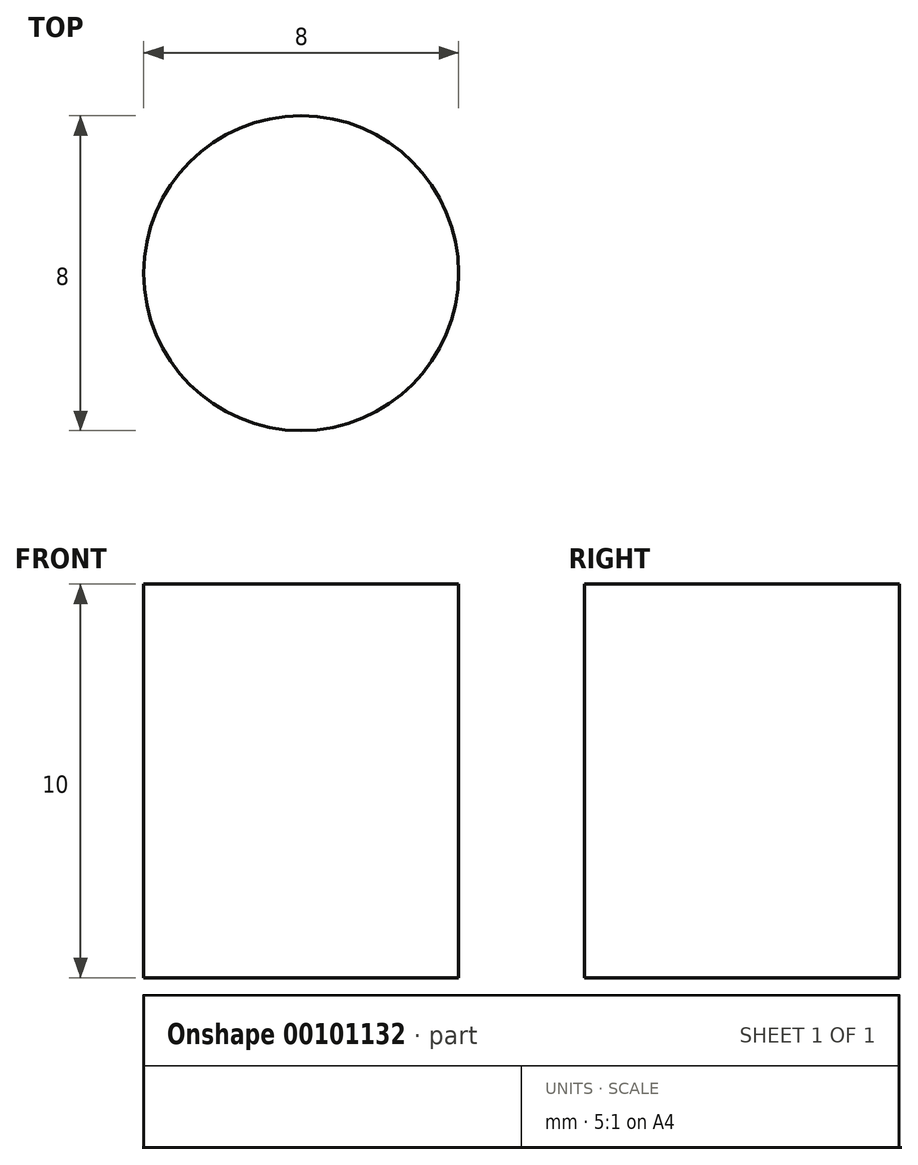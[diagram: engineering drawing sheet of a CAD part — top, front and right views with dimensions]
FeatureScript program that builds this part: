
annotation { "Feature Type Name" : "Feature", "Feature Type Description" : "" }
export const myFeature = defineFeature(function(context is Context, id is Id, definition is map)
    precondition{}
    {
        {
            var Q0;
            Q0=qCreatedBy(makeId("Top.planeOp"),FACE);
            var sketch = newSketch(context, id + "F0", { "sketchPlane" : qUnion([Q0])});
            skCircle(sketch, "E0", {"center": v(0, 0) * mm, "radius": 4 * mm});
            skSolve(sketch);
        }
        {
            var Q0;
            Q0 = qSketchRegion(id + "F0", true);
            extrude(context, id + "F1", {"entities" : qUnion([Q0]), "depth" : 10 * mm});
        }
    });
